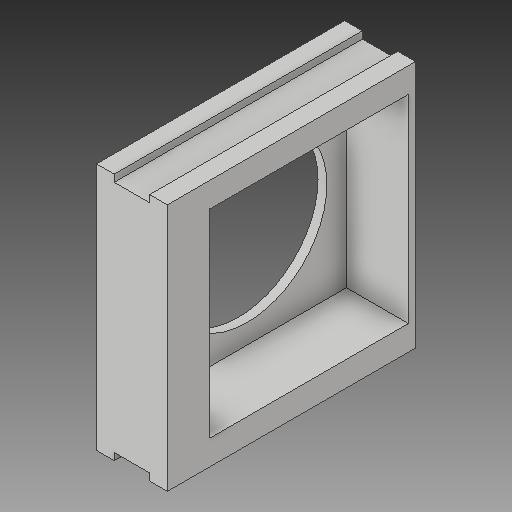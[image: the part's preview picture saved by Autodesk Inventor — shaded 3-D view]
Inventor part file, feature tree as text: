
AUTODESK INVENTOR PART (.ipt)
format: ipt  version: 2019 (Build 230136000, 136)  size: 189,440 bytes
history: native  units: mm
features: extrude x9, sketch x8, projected_geometry x1
ambient origin geometry x8: Origin, YZ Plane, XZ Plane, XY Plane, X Axis, Y Axis, Z Axis, Center Point
bodies: Solid1 (feature_tree)
feature tree (18):
  sketch  "Sketch1"  dims[d0=112.0mm d1=112.0mm]
  extrude  "Extrusion1"  Depth=112.0mm
  extrude  "Extrusion2"  Depth=160.0mm
  extrude  "Extrusion3"  Depth=5.0mm TaperAngle=0.0deg
  extrude  "Extrusion4"  Depth=10.0mm TaperAngle=0.0deg
  extrude  "Extrusion5"  Depth=10.0mm
  extrude  "Extrusion6"  Depth=10.0mm TaperAngle=0.0deg
  extrude  "Extrusion7"  Depth=10.0mm TaperAngle=0.0deg
  extrude  "Extrusion8"  Depth=20.0mm
  extrude  "Extrusion9"  Depth=4.0mm TaperAngle=0.0deg
  sketch  "Sketch2"  dims[d2=160.0mm d3=160.0mm]
  sketch  "Sketch3"  dims[d4=35.0mm d5=0.0mm d6=5.0mm d7=0.0mm]
  projected_geometry  "Projected Loop1"
  sketch  "Sketch4"  dims[d8=90.0mm d9=10.0mm d10=0.0mm]
  sketch  "Sketch5"  dims[d11=20.0mm d12=10.0mm]
  sketch  "Sketch6"  dims[d13=10.0mm d14=10.0mm d15=0.0mm]
  sketch  "Sketch7"  dims[d16=20.0mm d17=0.0mm d18=10.0mm d19=0.0mm]
  sketch  "Sketch8"  dims[d20=10.0mm d21=0.0mm d22=20.0mm d23=4.0mm d24=0.0mm d25=4.0mm d26=0.0mm]
